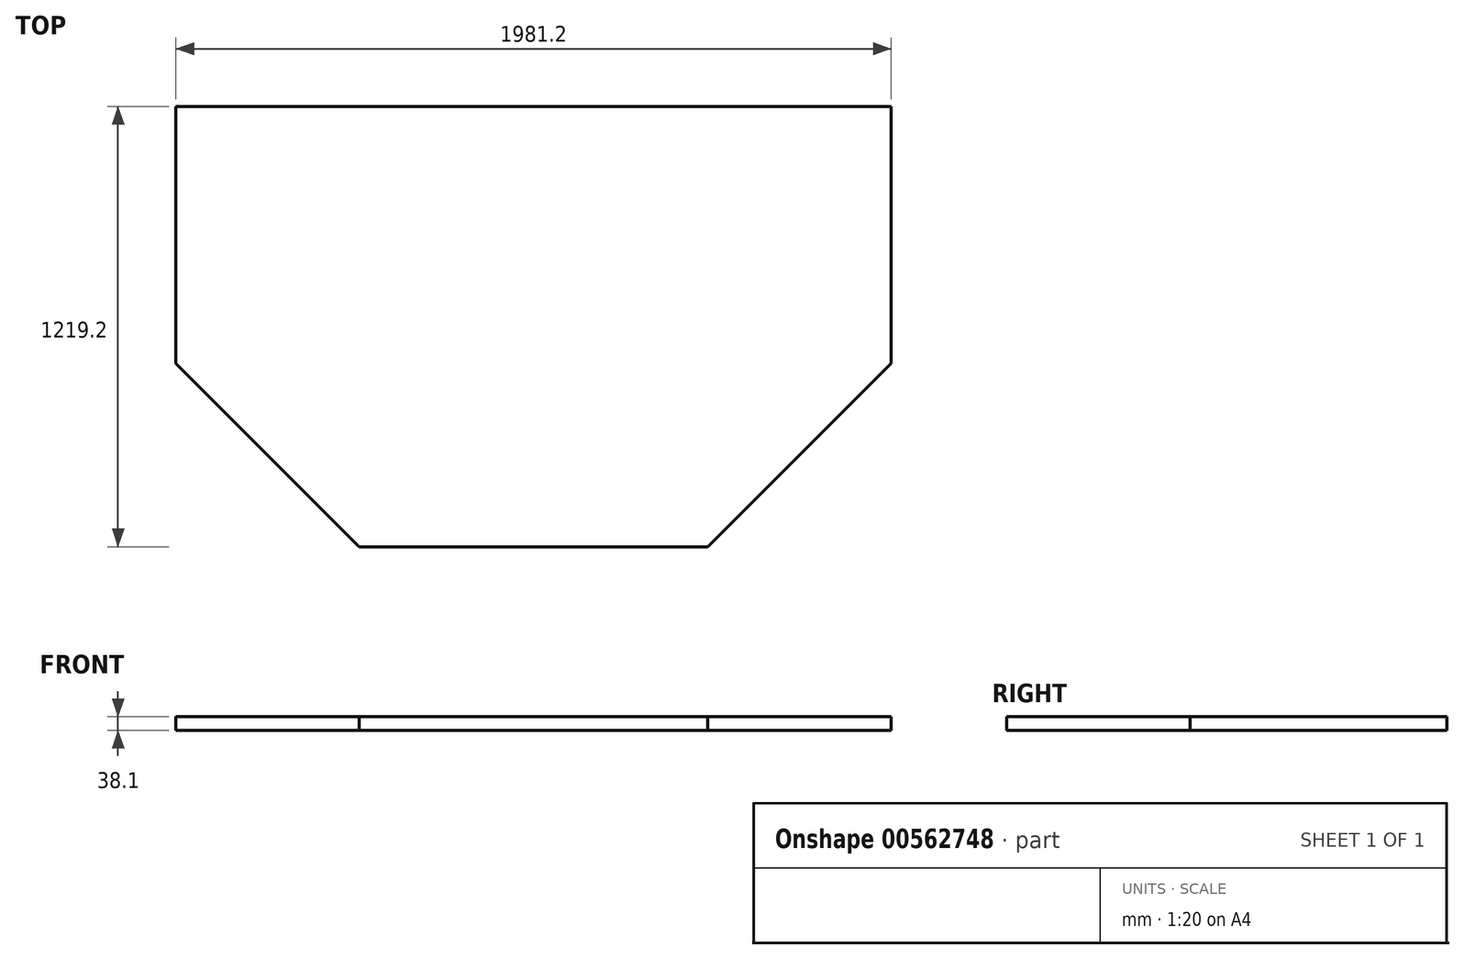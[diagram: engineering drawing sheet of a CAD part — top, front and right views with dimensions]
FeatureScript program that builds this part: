
annotation { "Feature Type Name" : "Feature", "Feature Type Description" : "" }
export const myFeature = defineFeature(function(context is Context, id is Id, definition is map)
    precondition{}
    {
        {
            var Q0;
            Q0=qCreatedBy(makeId("Top.planeOp"),FACE);
            var sketch = newSketch(context, id + "F0", { "sketchPlane" : qUnion([Q0])});
            skLineSegment(sketch, "E0.bottom", {"start": v(990.6, -609.6) * mm, "end": v(-990.6, -609.6) * mm});
            skLineSegment(sketch, "E0.top", {"start": v(990.6, 609.6) * mm, "end": v(-990.6, 609.6) * mm});
            skLineSegment(sketch, "E0.left", {"start": v(990.6, -609.6) * mm, "end": v(990.6, 609.6) * mm});
            skLineSegment(sketch, "E0.right", {"start": v(-990.6, -609.6) * mm, "end": v(-990.6, 609.6) * mm});
            skPoint(sketch, "E0.middle", {"position": v(0, 0) * mm});
            skSolve(sketch);
        }
        {
            var Q0;
            Q0 = qSketchRegion(id + "F0", true);
            extrude(context, id + "F1", {"entities" : qUnion([Q0]), "depth" : 38.1 * mm, "offsetDistance" : 25.4 * mm});
        }
        {
            var Q0;
            Q0=makeQuery(id+"F1.opExtrude","SWEPT_EDGE",EDGE,{"disambiguationData":[OSD([sQuery(id+"F0.wireOp",EDGE,"E0.bottom"),sQuery(id+"F0.wireOp",EDGE,"E0.left")])]});
            var Q1;
            Q1=makeQuery(id+"F1.opExtrude","SWEPT_EDGE",EDGE,{"disambiguationData":[OSD([sQuery(id+"F0.wireOp",EDGE,"E0.bottom"),sQuery(id+"F0.wireOp",EDGE,"E0.right")])]});
            chamfer(context, id + "F2", {"entities" : qUnion([Q0, Q1]), "width" : 508 * mm, "tangentPropagation" : true});
        }
    });
